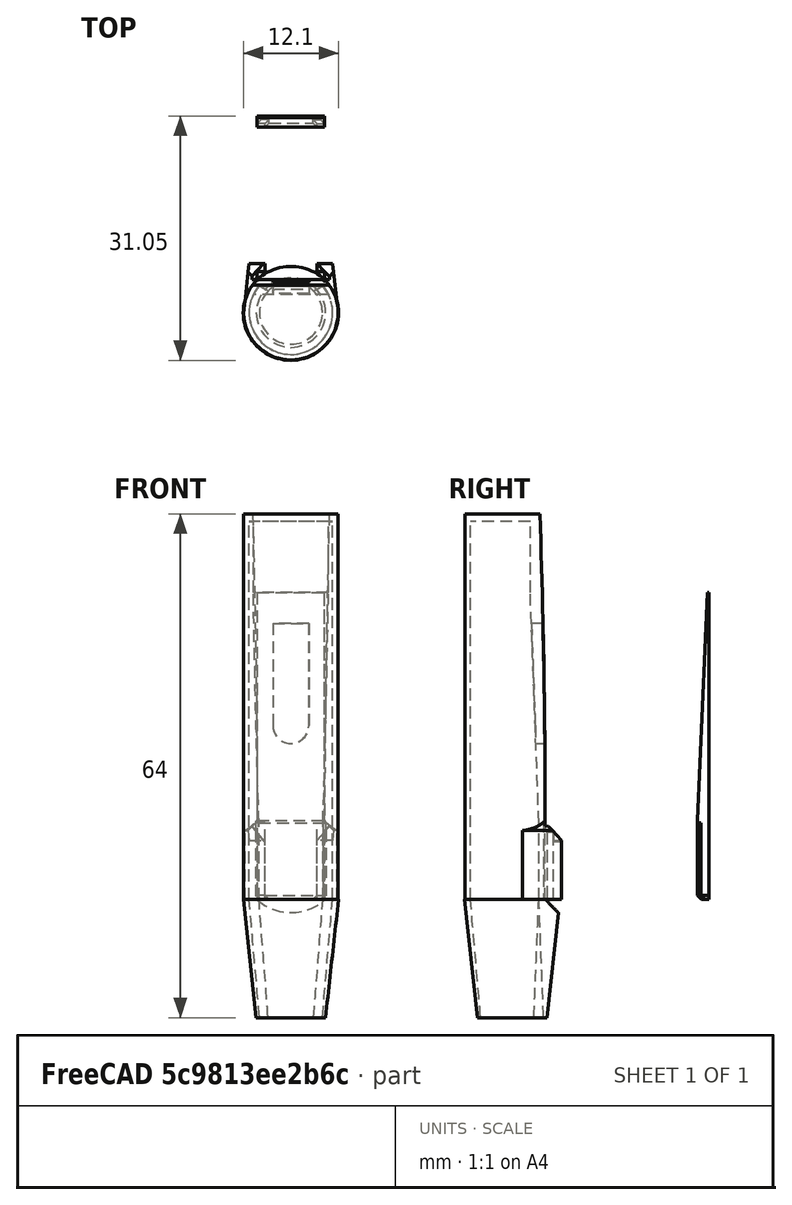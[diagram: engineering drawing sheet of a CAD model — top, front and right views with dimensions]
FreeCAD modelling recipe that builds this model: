
FCSTD DOCUMENT  (FreeCAD 1.0R39319 (Git))
Label: stroik
License: All rights reserved
LicenseURL: https://en.wikipedia.org/wiki/All_rights_reserved
objects: Sketcher::SketchObject×17, PartDesign::Pocket×10, PartDesign::Pad×4, PartDesign::Chamfer×3, App::VarSet×2, PartDesign::Body×2, Part::FeaturePython×1, PartDesign::FeatureBase×1, PartDesign::Mirrored×1, PartDesign::Plane×1, PartDesign::AdditiveLoft×1, PartDesign::ShapeBinder×1, Mesh::Feature×1
note: 97 computed .brp shape members not serialized (recipe doc carries the construction recipe); baked Part::Feature solids carry a one-line shape summary decoded from their .brp

FEATURE [Part::FeaturePython] Tube  # WARN: FeaturePython — macro-defined, semantics opaque (R4)
  AttacherType = Attacher::AttachEngine3D
  Height = 39
  InnerRadius = 5.3
  OuterRadius = 6
  Placement = pos=(0,0,0) rot=(0,1,0;1.5708rad)
  expr: Height = VarSet.leaf_len
  expr: InnerRadius = VarSet.d_inner
  expr: OuterRadius = VarSet.d_outer
FEATURE [PartDesign::FeatureBase] BaseFeature
  BaseFeature = -> Tube
  Suppressed = false
FEATURE [App::VarSet] VarSet
  d_inner = 5.3
  d_outer = 6
  d_outer_plug = 6.05
  leaf_end_thickness = 0.21
  leaf_gap = 1.5
  leaf_len = 39
  leaf_start_thickness = 1.44
  plug_inner_start = 4
  plug_len = 15
  plug_outer_start = 4.4
FEATURE [Sketcher::SketchObject] Sketch
  ArcFitTolerance = 1e-06
  AttachmentSupport = -> [YZ_Plane]
  ExternalGeometry = -> [BaseFeature]
  FullyConstrained = true
  MakeInternals = false
  MapMode = 5
  Placement = pos=(0,0,0) rot=(0.57735,0.57735,0.57735;2.0944rad)
  expr: Constraints[14] = VarSet.leaf_len / 4
  expr: Constraints[8] = VarSet.d_outer * 0.3
  sketch-geometry (6):
    g0: LineSegment StartX=6 StartY=39 StartZ=0 EndX=4.2 EndY=39 EndZ=0
    g1: LineSegment StartX=4.2 StartY=0 StartZ=0 EndX=6 EndY=0 EndZ=0
    g2: LineSegment StartX=6 StartY=0 StartZ=0 EndX=6 EndY=9.75 EndZ=0
    g3: LineSegment StartX=6 StartY=9.75 StartZ=0 EndX=6 EndY=39 EndZ=0
    g4: LineSegment StartX=4.2 StartY=39 StartZ=0 EndX=4.2 EndY=9.75 EndZ=0
    g5: LineSegment StartX=4.2 StartY=9.75 StartZ=0 EndX=4.2 EndY=0 EndZ=0
  constraints (17):
    c: Coincident(g0,g4)
    c: Coincident(g5,g1)
    c: Coincident(g1,g2)
    c: Coincident(g3,g0)
    c: Horizontal(g0)
    c: Horizontal(g1)
    c: Coincident(g0,g-3)
    c: PointOnObject(g5,g-4)
    c: DistanceX(g5,g1) = 1.8
    c: Coincident(g2,g3)
    c: Vertical(g2)
    c: Vertical(g3)
    c: Coincident(g4,g5)
    c: Vertical(g5)
    c: DistanceY(g2,g2) = 9.75
    c: Horizontal(g2,g4)
    c: Vertical(g4)
FEATURE [Sketcher::SketchObject] Sketch001
  ArcFitTolerance = 1e-06
  AttachmentSupport = -> [YZ_Plane]
  ExternalGeometry = -> [Sketch]
  FullyConstrained = true
  MakeInternals = false
  MapMode = 5
  Placement = pos=(0,0,0) rot=(0.57735,0.57735,0.57735;2.0944rad)
  expr: Constraints[12] = 0.8
  expr: Constraints[13] = VarSet.leaf_gap + 0.4 mm
  sketch-geometry (6):
    g0: LineSegment StartX=4.2 StartY=0 StartZ=0 EndX=3.4 EndY=0 EndZ=0
    g1: LineSegment StartX=3.4 StartY=0 StartZ=0 EndX=3.4 EndY=9.75 EndZ=0
    g2: LineSegment StartX=3.4 StartY=9.75 StartZ=0 EndX=2.3 EndY=39 EndZ=0
    g3: LineSegment StartX=2.3 StartY=39 StartZ=0 EndX=4.2 EndY=39 EndZ=0
    g4: LineSegment StartX=4.2 StartY=39 StartZ=0 EndX=4.2 EndY=9.75 EndZ=0
    g5: LineSegment StartX=4.2 StartY=9.75 StartZ=0 EndX=4.2 EndY=0 EndZ=0
  constraints (15):
    c: Coincident(g-4,g0)
    c: PointOnObject(g0,g-1)
    c: Coincident(g0,g1)
    c: Vertical(g1)
    c: Coincident(g1,g2)
    c: Coincident(g2,g3)
    c: Coincident(g3,g-3)
    c: Horizontal(g3)
    c: Coincident(g3,g4)
    c: Coincident(g4,g-4)
    c: Coincident(g4,g5)
    c: Coincident(g5,g0)
    c: DistanceX(g1,g4) = 0.8
    c: DistanceX(g2,g3) = 1.9
    c: Horizontal(g1,g4)
FEATURE [PartDesign::Pocket] Pocket  label="1 ścięcie"
  BaseFeature = -> BaseFeature
  Direction = (-1,0,0)
  Length = 5
  Length2 = 5
  Midplane = true
  Profile = -> Sketch
  ReferenceAxis = -> Sketch [N_Axis]
  Refine = true
  Suppressed = false
  Type = 1
FEATURE [PartDesign::Pad] Pad  label="uzupełnienie"
  AlongSketchNormal = false
  BaseFeature = -> Pocket
  Direction = (1,0,0)
  Length = 13
  Length2 = 10
  Midplane = true
  Profile = -> Sketch001
  ReferenceAxis = -> Sketch001 [N_Axis]
  Refine = true
  Suppressed = false
  Type = 1
  UpToShape = -> [Pocket]
FEATURE [PartDesign::Mirrored] Mirrored
  BaseFeature = -> Pad
  MirrorPlane = -> YZ_Plane
  Originals = -> [Pad]
  Refine = true
  Suppressed = false
  TransformMode = 0
FEATURE [Sketcher::SketchObject] Sketch002
  ArcFitTolerance = 1e-06
  AttachmentSupport = -> [Mirrored]
  ExternalGeometry = -> [Mirrored]
  FullyConstrained = true
  MakeInternals = false
  MapMode = 5
  Placement = pos=(0,4.2,0) rot=(0,0.707107,0.707107;3.14159rad)
  expr: Constraints[11] = VarSet.d_outer / 3
  expr: Constraints[8] = VarSet.leaf_len / 10
  expr: Constraints[9] = VarSet.leaf_len / 3
  sketch-geometry (4):
    g0: LineSegment StartX=2.28486 StartY=22.1 StartZ=0 EndX=2.28486 EndY=35.1 EndZ=0
    g1: LineSegment StartX=2.28486 StartY=35.1 StartZ=0 EndX=-2.28486 EndY=35.1 EndZ=0
    g2: LineSegment StartX=-2.28486 StartY=35.1 StartZ=0 EndX=-2.28486 EndY=22.1 EndZ=0
    g3: ArcOfCircle CenterX=0 CenterY=22.1 CenterZ=0 NormalX=0 NormalY=0 NormalZ=1 AngleXU=0 Radius=2.28486 StartAngle=3.14159 EndAngle=6.28319
  constraints (12):
    c: Coincident(g0,g1)
    c: Coincident(g1,g2)
    c: Coincident(g3,g2)
    c: Coincident(g3,g0)
    c: PointOnObject(g3,g-2)
    c: Horizontal(g0,g2)
    c: Horizontal(g2,g3)
    c: Symmetric(g0,g1,g-2)
    c: DistanceY(g1,g-7) = 3.9
    c: DistanceY(g3,g1) = 13
    c: Vertical(g1,g2)
    c: DistanceX(g0,g-6) = 2
FEATURE [PartDesign::Pocket] Pocket001  label="dziurka"
  BaseFeature = -> Mirrored
  Direction = (0,-1,2e-16)
  Length = 2.65
  Length2 = 5
  Profile = -> Sketch002
  ReferenceAxis = -> Sketch002 [N_Axis]
  Refine = true
  Suppressed = false
  Type = 0
  expr: Length = VarSet.d_inner / 2
FEATURE [Sketcher::SketchObject] Sketch003
  ArcFitTolerance = 1e-06
  AttachmentSupport = -> [Pocket001]
  ExternalGeometry = -> [Pocket001]
  FullyConstrained = true
  MakeInternals = false
  MapMode = 5
  Placement = pos=(0,0,39) rot=(0,0,1;0rad)
  sketch-geometry (2):
    g0: ArcOfCircle CenterX=0 CenterY=0 CenterZ=0 NormalX=0 NormalY=0 NormalZ=1 AngleXU=0 Radius=6 StartAngle=2.3662 EndAngle=7.05858
    g1: LineSegment StartX=-4.28486 StartY=4.2 StartZ=0 EndX=4.28486 EndY=4.2 EndZ=0
  constraints (5):
    c: Coincident(g0,g-1)
    c: Coincident(g0,g-4)
    c: Coincident(g1,g0)
    c: Coincident(g1,g0)
    c: Horizontal(g1)
FEATURE [PartDesign::Pad] Pad001  label="zaślepka"
  BaseFeature = -> Pocket001
  Direction = (0,0,1)
  Length = 10
  Length2 = 10
  Profile = -> Sketch003
  ReferenceAxis = -> Sketch003 [N_Axis]
  Refine = true
  Suppressed = false
  Type = 0
FEATURE [Sketcher::SketchObject] Sketch004
  ArcFitTolerance = 1e-06
  AttachmentSupport = -> [Pad001]
  ExternalGeometry = -> [Pad001]
  FullyConstrained = true
  MakeInternals = false
  MapMode = 5
  Placement = pos=(0,0,0) rot=(1,0,0;3.14159rad)
  expr: Constraints[4] = VarSet.d_outer_plug
  expr: Constraints[7] = VarSet.d_inner
  sketch-geometry (3):
    g0: ArcOfCircle CenterX=0 CenterY=0 CenterZ=0 NormalX=0 NormalY=0 NormalZ=1 AngleXU=0 Radius=5.3 StartAngle=5.58672 EndAngle=10.1212
    g1: LineSegment StartX=-4.06571 StartY=-3.4 StartZ=0 EndX=4.06571 EndY=-3.4 EndZ=0
    g2: Circle CenterX=0 CenterY=0 CenterZ=0 NormalX=0 NormalY=0 NormalZ=1 AngleXU=0 Radius=6.05
  constraints (8):
    c: Coincident(g1,g0)
    c: Horizontal(g1)
    c: Coincident(g2,g0)
    c: Coincident(g-1,g0)
    c: Radius(g2) = 6.05
    c: Horizontal(g0,g-6)
    c: Coincident(g1,g0)
    c: Radius(g0) = 5.3
FEATURE [PartDesign::Plane] DatumPlane
  AttachmentOffset = pos=(0,0,15) rot=(0,0,1;0rad)
  AttachmentSupport = -> [Pocket001]
  Length = 60
  MapMode = 5
  Placement = pos=(0,0,-15) rot=(1,0,0;3.14159rad)
  ResizeMode = 0
  Width = 60
  expr: .AttachmentOffset.Base.z = VarSet.plug_len
FEATURE [Sketcher::SketchObject] Sketch005
  ArcFitTolerance = 1e-06
  AttachmentSupport = -> [DatumPlane]
  ExternalGeometry = -> [Sketch004,Pad001]
  FullyConstrained = true
  MakeInternals = false
  MapMode = 5
  Placement = pos=(0,0,-15) rot=(1,0,0;3.14159rad)
  expr: Constraints[2] = VarSet.plug_inner_start
  expr: Constraints[3] = VarSet.plug_outer_start
  sketch-geometry (2):
    g0: Circle CenterX=0 CenterY=0 CenterZ=0 NormalX=0 NormalY=0 NormalZ=1 AngleXU=0 Radius=4
    g1: Circle CenterX=0 CenterY=0 CenterZ=0 NormalX=0 NormalY=0 NormalZ=1 AngleXU=0 Radius=4.4
  constraints (4):
    c: Coincident(g0,g-1)
    c: Coincident(g1,g0)
    c: Radius(g0) = 4
    c: Radius(g1) = 4.4
FEATURE [PartDesign::AdditiveLoft] AdditiveLoft  label="dziubek"
  BaseFeature = -> Pad001
  Closed = false
  Profile = -> Sketch005
  Refine = true
  Ruled = false
  Sections = -> [Sketch004]
  Suppressed = false
FEATURE [Sketcher::SketchObject] Sketch006
  ArcFitTolerance = 1e-06
  AttachmentSupport = -> [Pad001]
  ExternalGeometry = -> [Pad001]
  FullyConstrained = false
  MakeInternals = false
  MapMode = 5
  Placement = pos=(0,0,0) rot=(1,0,0;3.14159rad)
  expr: Constraints[24] = 1.05 mm
  sketch-geometry (16):
    g0: LineSegment StartX=4.28486 StartY=-4.2 StartZ=0 EndX=6 EndY=0 EndZ=0
    g1: LineSegment StartX=6 StartY=0 StartZ=0 EndX=5.28986 EndY=-6.25 EndZ=0
    g2: LineSegment StartX=5.28986 StartY=-6.25 StartZ=0 EndX=3.28986 EndY=-6.25 EndZ=0
    g3: LineSegment StartX=3.28986 StartY=-6.25 StartZ=0 EndX=3.28986 EndY=-5.25 EndZ=0
    g4: LineSegment StartX=3.28986 StartY=-5.25 StartZ=0 EndX=4.28986 EndY=-5.25 EndZ=0
    g5: LineSegment StartX=-5.28986 StartY=-6.25 StartZ=0 EndX=-3.28986 EndY=-6.25 EndZ=0
    g6: LineSegment StartX=-6 StartY=0 StartZ=0 EndX=-5.28986 EndY=-6.25 EndZ=0
    g7: LineSegment StartX=-4.28486 StartY=-4.2 StartZ=0 EndX=-6 EndY=0 EndZ=0
    g8: LineSegment StartX=-3.28986 StartY=-5.25 StartZ=0 EndX=-4.28986 EndY=-5.25 EndZ=0
    g9: LineSegment StartX=-3.28986 StartY=-6.25 StartZ=0 EndX=-3.28986 EndY=-5.25 EndZ=0
    g10: LineSegment StartX=4.28986 StartY=-5.25 StartZ=0 EndX=4.28986 EndY=-4.2 EndZ=0
    g11: LineSegment StartX=-4.28986 StartY=-5.25 StartZ=0 EndX=-4.28986 EndY=-4.2 EndZ=0
    g12: LineSegment StartX=4.28986 StartY=-4.2 StartZ=0 EndX=4.28717 EndY=-4.19654 EndZ=0
    g13: LineSegment StartX=4.28717 StartY=-4.19654 StartZ=0 EndX=4.28486 EndY=-4.2 EndZ=0
    g14: LineSegment StartX=-4.28986 StartY=-4.2 StartZ=0 EndX=-4.28627 EndY=-4.19642 EndZ=0
    g15: LineSegment StartX=-4.28627 StartY=-4.19642 StartZ=0 EndX=-4.28486 EndY=-4.2 EndZ=0
  constraints (36):
    c: Coincident(g-5,g0)
    c: Coincident(g0,g1)
    c: Coincident(g1,g2)
    c: Horizontal(g2)
    c: Coincident(g2,g3)
    c: Vertical(g3)
    c: Coincident(g3,g4)
    c: Horizontal(g4)
    c: Coincident(g4,g10)
    c: Coincident(g13,g0)
    c: Coincident(g7,g6)
    c: Coincident(g6,g5)
    c: Coincident(g5,g9)
    c: Vertical(g9)
    c: Coincident(g9,g8)
    c: Horizontal(g8)
    c: Coincident(g8,g11)
    c: Coincident(g15,g7)
    c: Symmetric(g2,g5,g-2)
    c: DistanceX(g4,g4) = 1
    c: Symmetric(g4,g11,g-2)
    c: Symmetric(g0,g6,g-2)
    c: DistanceY(g3,g3) = 1
    c: Symmetric(g7,g0,g-2)
    c: DistanceY(g10,g13) = 1.05
    c: DistanceX(g2,g2) = 2
    c: Coincident(g0,g-5)
    c: Symmetric(g5,g1,g-2)
    c: Coincident(g10,g12)
    c: Vertical(g10)
    c: Horizontal(g10,g0)
    c: DistanceX(g13,g12) = 0.005
    c: Coincident(g11,g14)
    c: Symmetric(g11,g10,g-2)
    c: Coincident(g12,g13)
    c: Coincident(g14,g15)
FEATURE [PartDesign::Pad] Pad002  label="uchwyt na listek"
  BaseFeature = -> AdditiveLoft
  Direction = (0,0,-1)
  Length = 9.75
  Length2 = 10
  Profile = -> Sketch006
  ReferenceAxis = -> Sketch006 [N_Axis]
  Refine = true
  Reversed = true
  Suppressed = false
  Type = 0
  expr: Length = VarSet.leaf_len / 4
FEATURE [Sketcher::SketchObject] Sketch009
  ArcFitTolerance = 1e-06
  AttachmentSupport = -> [YZ_Plane]
  ExternalGeometry = -> [Pad001]
  FullyConstrained = false
  MakeInternals = false
  MapMode = 5
  Placement = pos=(0,0,0) rot=(0.57735,0.57735,0.57735;2.0944rad)
  expr: .Constraints.gap = VarSet.leaf_gap
  expr: Constraints[19] = 3 / 4 * VarSet.leaf_len * 3 / 2
  expr: Constraints[1] = VarSet.leaf_len / 4
  expr: Constraints[20] = 3 / 4 * VarSet.leaf_len * 3
  sketch-geometry (13):
    g0: GeomPoint X=4.2 Y=9.75 Z=0
    g1: Circle [constr] CenterX=4.2 CenterY=9.75 CenterZ=0 NormalX=0 NormalY=0 NormalZ=1 AngleXU=0 Radius=1
    g2: Circle [constr] CenterX=4.2 CenterY=53.625 CenterZ=0 NormalX=0 NormalY=0 NormalZ=1 AngleXU=0 Radius=1
    g3: Circle [constr] CenterX=0.846497 CenterY=97.5 CenterZ=0 NormalX=0 NormalY=0 NormalZ=1 AngleXU=0 Radius=1
    g4: BSplineCurve PolesCount=3 KnotsCount=2 Degree=2 IsPeriodic=0
    g5: GeomPoint [constr] X=4.2 Y=9.75 Z=0
    g6: GeomPoint [constr] X=0.846497 Y=97.5 Z=0
    g7: LineSegment [constr] StartX=0.846497 StartY=97.5 StartZ=0 EndX=4.2 EndY=9.75 EndZ=0
    g8: LineSegment StartX=104.2 StartY=41.25 StartZ=0 EndX=104.2 EndY=9.75 EndZ=0
    g9: LineSegment StartX=104.2 StartY=9.75 StartZ=0 EndX=4.2 EndY=9.75 EndZ=0
    g10: LineSegment StartX=0.846497 StartY=97.5 StartZ=0 EndX=0.846497 EndY=90 EndZ=0
    g11: LineSegment StartX=0.846497 StartY=90 StartZ=0 EndX=104.2 EndY=41.25 EndZ=0
    g12: LineSegment [constr] StartX=4.2 StartY=49 StartZ=0 EndX=2.7 EndY=49 EndZ=0
  constraints (29):
    c: PointOnObject(g0,g-3)
    c: DistanceY(g-3,g0) = 9.75
    c: Weight(g1) = 1
    c: Equal(g1,g2)
    c: Equal(g1,g3)
    c: InternalAlignment(g1,g4)
    c: InternalAlignment(g2,g4)
    c: InternalAlignment(g3,g4)
    c: InternalAlignment(g5,g4)
    c: InternalAlignment(g6,g4)
    c: Coincident(g1,g0)
    c: Coincident(g7,g4)
    c: Coincident(g7,g4)
    c: Vertical(g8)
    c: Coincident(g8,g9)
    c: Coincident(g9,g0)
    c: Horizontal(g9)
    c: DistanceX(g9,g9) = 100
    c: Vertical(g-3,g2)
    c: DistanceY(g0,g2) = 43.875
    c: DistanceY(g0,g4) = 87.75
    c: Coincident(g10,g4)
    c: Vertical(g10)
    c: Coincident(g11,g10)
    c: Coincident(g11,g8)
    c: Coincident(g12,g-3)
    c: PointOnObject(g12,g7)
    c: Horizontal(g12)
    c: DistanceX(g12,g12) = 1.5  'gap'
FEATURE [PartDesign::Pocket] Pocket003  label="2 ścięcie"
  BaseFeature = -> Pad002
  Direction = (-1,0,0)
  Length = 100
  Length2 = 5
  Midplane = true
  Profile = -> Sketch009
  ReferenceAxis = -> Sketch009 [N_Axis]
  Refine = true
  Suppressed = false
  Type = 0
FEATURE [PartDesign::ShapeBinder] ShapeBinder
  Support = -> [Mirrored]
  TraceSupport = false
FEATURE [Sketcher::SketchObject] Sketch010  label="main shape"
  ArcFitTolerance = 1e-06
  AttachmentSupport = -> [XZ_Plane001]
  ExternalGeometry = -> [ShapeBinder]
  FullyConstrained = true
  MakeInternals = false
  MapMode = 5
  Placement = pos=(0,0,0) rot=(1,0,0;1.5708rad)
  expr: Constraints[6] = VarSet.leaf_len / 4
  expr: Constraints[9] = VarSet.leaf_len
  sketch-geometry (6):
    g0: LineSegment StartX=-4.28486 StartY=0 StartZ=0 EndX=4.28486 EndY=9e-16 EndZ=0
    g1: LineSegment StartX=4.28486 StartY=9e-16 StartZ=0 EndX=4.28486 EndY=9.75 EndZ=0
    g2: LineSegment StartX=-4.28486 StartY=9.75 StartZ=0 EndX=-4.28486 EndY=0 EndZ=0
    g3: LineSegment StartX=4.28486 StartY=9.75 StartZ=0 EndX=4.28486 EndY=39 EndZ=0
    g4: LineSegment StartX=-4.28486 StartY=9.75 StartZ=0 EndX=-4.28486 EndY=39 EndZ=0
    g5: LineSegment StartX=-4.28486 StartY=39 StartZ=0 EndX=4.28486 EndY=39 EndZ=0
  constraints (15):
    c: Coincident(g0,g1)
    c: Coincident(g2,g0)
    c: Vertical(g1)
    c: Vertical(g2)
    c: Coincident(g0,g-3)
    c: Coincident(g0,g-3)
    c: DistanceY(g1,g1) = 9.75
    c: Coincident(g3,g1)
    c: Symmetric(g3,g4,g-2)
    c: DistanceY(g0,g3) = 39
    c: Horizontal(g2,g1)
    c: Coincident(g4,g2)
    c: Coincident(g5,g4)
    c: Coincident(g5,g3)
    c: Vertical(g3)
FEATURE [PartDesign::Pad] Pad003
  Direction = (0,-1,2e-16)
  Length = 1.44
  Length2 = 10
  Placement = pos=(0,0,0) rot=(1,0,0;1.5708rad)
  Profile = -> Sketch010
  ReferenceAxis = -> Sketch010 [N_Axis]
  Refine = true
  Suppressed = false
  Type = 0
  expr: Length = VarSet.leaf_start_thickness
FEATURE [Sketcher::SketchObject] Sketch011
  ArcFitTolerance = 1e-06
  AttachmentSupport = -> [Pad003]
  ExternalGeometry = -> [Pad003]
  FullyConstrained = true
  MakeInternals = false
  MapMode = 5
  Placement = pos=(0,0,4e-16) rot=(1,0,0;3.14159rad)
  sketch-geometry (8):
    g0: LineSegment StartX=-3.28486 StartY=1.44 StartZ=0 EndX=-3.28486 EndY=1 EndZ=0
    g1: LineSegment StartX=-3.28486 StartY=1 StartZ=0 EndX=-8.28486 EndY=1 EndZ=0
    g2: LineSegment StartX=-8.28486 StartY=1 StartZ=0 EndX=-8.28486 EndY=4.94104 EndZ=0
    g3: LineSegment StartX=-8.28486 StartY=4.94104 StartZ=0 EndX=-3.28486 EndY=1.44 EndZ=0
    g4: LineSegment StartX=8.28486 StartY=4.94104 StartZ=0 EndX=3.28486 EndY=1.44 EndZ=0
    g5: LineSegment StartX=3.28486 StartY=1.44 StartZ=0 EndX=3.28486 EndY=1 EndZ=0
    g6: LineSegment StartX=3.28486 StartY=1 StartZ=0 EndX=8.28486 EndY=1 EndZ=0
    g7: LineSegment StartX=8.28486 StartY=1 StartZ=0 EndX=8.28486 EndY=4.94104 EndZ=0
  constraints (21):
    c: PointOnObject(g0,g-3)
    c: Vertical(g0)
    c: Coincident(g0,g1)
    c: Horizontal(g1)
    c: Coincident(g1,g2)
    c: Vertical(g2)
    c: Coincident(g2,g3)
    c: Coincident(g3,g0)
    c: DistanceX(g-4,g0) = 1
    c: Vertical(g5)
    c: Coincident(g5,g6)
    c: Coincident(g6,g7)
    c: Coincident(g7,g4)
    c: Coincident(g4,g5)
    c: Symmetric(g4,g0,g-2)
    c: Symmetric(g5,g0,g-2)
    c: Symmetric(g6,g1,g-2)
    c: Symmetric(g4,g2,g-2)
    c: DistanceY(g-5,g0) = 1
    c: Angle(g-3,g3) = 2.53073
    c: DistanceX(g1,g1) = 5
FEATURE [PartDesign::Pocket] Pocket004  label="uchwyt"
  BaseFeature = -> Pad003
  Direction = (0,0,1)
  Length = 9.75
  Length2 = 5
  Placement = pos=(0,0,0) rot=(1,0,0;1.5708rad)
  Profile = -> Sketch011
  ReferenceAxis = -> Sketch011 [N_Axis]
  Refine = true
  Suppressed = false
  Type = 0
  expr: Length = VarSet.leaf_len / 4
FEATURE [Sketcher::SketchObject] Sketch012
  ArcFitTolerance = 1e-06
  AttachmentSupport = -> [Pocket004]
  FullyConstrained = true
  MakeInternals = false
  MapMode = 5
  Placement = pos=(-4.28486,0,-2.78e-14) rot=(0.707107,0,-0.707107;3.14159rad)
  expr: Constraints[0] = VarSet.d_inner + 0.4 mm
  expr: Constraints[5] = VarSet.leaf_end_thickness
  sketch-geometry (3):
    g0: LineSegment StartX=-39.052 StartY=0.21 StartZ=0 EndX=-10.0388 EndY=1.44 EndZ=0
    g1: LineSegment StartX=-39.052 StartY=0.21 StartZ=0 EndX=-39.052 EndY=14.04 EndZ=0
    g2: LineSegment StartX=-39.052 StartY=14.04 StartZ=0 EndX=-10.0388 EndY=1.44 EndZ=0
  constraints (8):
    c: DistanceX(g0,g-3) = 5.7
    c: Coincident(g1,g0)
    c: Vertical(g1)
    c: Coincident(g2,g1)
    c: Coincident(g2,g0)
    c: DistanceY(g-4,g0) = 0.21
    c: Coincident(g0,g-3)
    c: DistanceY(g1,g1) = 13.83
FEATURE [PartDesign::Pocket] Pocket005  label="Pochylenie"
  BaseFeature = -> Pocket004
  Direction = (1,0,6.4e-15)
  Length = 5
  Length2 = 5
  Placement = pos=(0,0,0) rot=(1,0,0;1.5708rad)
  Profile = -> Sketch012
  ReferenceAxis = -> Sketch012 [N_Axis]
  Refine = true
  Suppressed = false
  Type = 1
FEATURE [PartDesign::Chamfer] Chamfer
  Angle = 45
  Base = -> Pocket003 [?Edge89,?Edge77]
  BaseFeature = -> Pocket003
  ChamferType = 0
  FlipDirection = false
  Refine = true
  Size = 2
  Size2 = 1
  SupportTransform = false
  Suppressed = true
  UseAllEdges = false
FEATURE [Sketcher::SketchObject] Sketch013
  ArcFitTolerance = 1e-06
  AttachmentSupport = -> [YZ_Plane]
  FullyConstrained = true
  MakeInternals = false
  MapMode = 5
  Placement = pos=(0,0,0) rot=(0.57735,0.57735,0.57735;2.0944rad)
  sketch-geometry (3):
    g0: LineSegment StartX=4.2 StartY=0 StartZ=0 EndX=18.3421 EndY=-14.1421 EndZ=0
    g1: LineSegment StartX=18.3421 StartY=-14.1421 StartZ=0 EndX=18.3421 EndY=1.8e-15 EndZ=0
    g2: LineSegment StartX=18.3421 StartY=1.8e-15 StartZ=0 EndX=4.2 EndY=0 EndZ=0
  constraints (8):
    c: Coincident(g-3,g0)
    c: Coincident(g0,g1)
    c: Vertical(g1)
    c: Coincident(g1,g2)
    c: Coincident(g2,g0)
    c: Angle(g-2,g0) = 0.785398
    c: Distance(g0,g0) = 20
    c: Angle(g0,g2) = 0.785398
FEATURE [PartDesign::Pocket] Pocket006
  BaseFeature = -> Chamfer
  Direction = (-1,0,0)
  Length = 5
  Length2 = 5
  Midplane = true
  Profile = -> Sketch013
  ReferenceAxis = -> Sketch013 [N_Axis]
  Refine = true
  Suppressed = false
  Type = 1
FEATURE [Sketcher::SketchObject] Sketch014
  ArcFitTolerance = 1e-06
  AttachmentSupport = -> [Pocket006]
  ExternalGeometry = -> [Mirrored]
  FullyConstrained = true
  MakeInternals = false
  MapMode = 5
  Placement = pos=(0,0,39) rot=(1,0,0;3.14159rad)
  sketch-geometry (2):
    g0: ArcOfCircle CenterX=0 CenterY=0 CenterZ=0 NormalX=0 NormalY=0 NormalZ=1 AngleXU=0 Radius=5.3 StartAngle=5.8343 EndAngle=9.87366
    g1: LineSegment StartX=4.77493 StartY=-2.3 StartZ=0 EndX=-4.77493 EndY=-2.3 EndZ=0
  constraints (5):
    c: Coincident(g0,g-1)
    c: Coincident(g0,g-4)
    c: Coincident(g1,g0)
    c: Coincident(g1,g0)
    c: Horizontal(g1)
FEATURE [PartDesign::Pocket] Pocket007
  BaseFeature = -> Pocket006
  Direction = (0,0,1)
  Length = 9
  Length2 = 5
  Profile = -> Sketch014
  ReferenceAxis = -> Sketch014 [N_Axis]
  Refine = true
  Suppressed = false
  Type = 0
FEATURE [App::VarSet] VarSet001  label="VarSet009"
  d_inner = 5.3
  d_outer = 6
  d_outer_plug = 6
  leaf_angle = 0
  leaf_angle2 = 1.6
  leaf_end_thickness = 0.2
  leaf_len = 39
  leaf_start_thickness = 1.45
  plug_inner_start = 4
  plug_len = 15
  plug_outer_start = 4.4
FEATURE [Sketcher::SketchObject] Sketch015
  ArcFitTolerance = 1e-06
  AttachmentSupport = -> [Pocket007]
  FullyConstrained = true
  MakeInternals = false
  MapMode = 5
  Placement = pos=(0,6.25,0) rot=(0,0.707107,0.707107;3.14159rad)
FEATURE [Sketcher::SketchObject] Sketch016
  ArcFitTolerance = 1e-06
  AttachmentSupport = -> [Pocket007]
  ExternalGeometry = -> [Pocket007]
  FullyConstrained = false
  MakeInternals = false
  MapMode = 5
  Placement = pos=(0,6.25,0) rot=(0,0.707107,0.707107;3.14159rad)
  sketch-geometry (6):
    g0: LineSegment StartX=-5.28986 StartY=9.75 StartZ=0 EndX=-2.018 EndY=6.06813 EndZ=0
    g1: LineSegment StartX=-2.018 StartY=6.06813 StartZ=0 EndX=-2.018 EndY=11.9722 EndZ=0
    g2: LineSegment StartX=-2.018 StartY=11.9722 StartZ=0 EndX=-5.28986 EndY=9.75 EndZ=0
    g3: LineSegment StartX=5.28986 StartY=9.75 StartZ=0 EndX=2.26844 EndY=6.06813 EndZ=0
    g4: LineSegment StartX=2.26844 StartY=6.06813 StartZ=0 EndX=2.26844 EndY=11.9722 EndZ=0
    g5: LineSegment StartX=2.26844 StartY=11.9722 StartZ=0 EndX=5.28986 EndY=9.75 EndZ=0
  constraints (12):
    c: Coincident(g-3,g0)
    c: Coincident(g0,g1)
    c: Vertical(g1)
    c: Coincident(g1,g2)
    c: Coincident(g2,g0)
    c: Coincident(g-4,g3)
    c: Coincident(g3,g4)
    c: Vertical(g4)
    c: Coincident(g4,g5)
    c: Coincident(g5,g3)
    c: Horizontal(g0,g3)
    c: Horizontal(g1,g4)
FEATURE [PartDesign::Pocket] Pocket008
  BaseFeature = -> Pocket007
  Direction = (0,-1,2e-16)
  Length = 5
  Length2 = 5
  Profile = -> Sketch016
  ReferenceAxis = -> Sketch016 [N_Axis]
  Refine = true
  Suppressed = false
  Type = 2
FEATURE [Sketcher::SketchObject] Sketch017
  ArcFitTolerance = 1e-06
  AttachmentSupport = -> [Pocket008]
  FullyConstrained = false
  MakeInternals = false
  MapMode = 5
  Placement = pos=(4.28986,0,0) rot=(0.57735,-0.57735,-0.57735;2.0944rad)
  sketch-geometry (3):
    g0: LineSegment StartX=-4.21102 StartY=9.75787 StartZ=0 EndX=-7.69576 EndY=5.94234 EndZ=0
    g1: LineSegment StartX=-7.69576 StartY=5.94234 StartZ=0 EndX=-7.9348 EndY=11.8707 EndZ=0
    g2: LineSegment StartX=-7.9348 StartY=11.8707 StartZ=0 EndX=-4.21102 EndY=9.75787 EndZ=0
  constraints (3):
    c: Coincident(g0,g1)
    c: Coincident(g1,g2)
    c: Coincident(g2,g0)
FEATURE [PartDesign::Pocket] Pocket009
  BaseFeature = -> Pocket008
  Direction = (1,0,0)
  Length = 5
  Length2 = 5
  Midplane = true
  Profile = -> Sketch017
  ReferenceAxis = -> Sketch017 [N_Axis]
  Refine = true
  Suppressed = false
  Type = 1
FEATURE [PartDesign::Chamfer] Chamfer001
  Angle = 45
  Base = -> Pocket009 [Edge62,Edge80]
  BaseFeature = -> Pocket009
  ChamferType = 0
  FlipDirection = false
  Refine = true
  Size = 1
  Size2 = 1
  SupportTransform = false
  Suppressed = false
  UseAllEdges = false
FEATURE [Sketcher::SketchObject] Sketch018
  ArcFitTolerance = 1e-06
  AttachmentSupport = -> [Chamfer001]
  ExternalGeometry = -> [Chamfer001]
  FullyConstrained = true
  MakeInternals = false
  MapMode = 5
  Placement = pos=(0,0,0) rot=(1,0,0;3.14159rad)
  sketch-geometry (2):
    g0: Circle CenterX=4.28986 CenterY=-4.2 CenterZ=0 NormalX=0 NormalY=0 NormalZ=1 AngleXU=0 Radius=0.2
    g1: Circle CenterX=-4.28986 CenterY=-4.2 CenterZ=0 NormalX=0 NormalY=0 NormalZ=1 AngleXU=0 Radius=0.2
  constraints (4):
    c: Coincident(g0,g-4)
    c: Diameter(g0) = 0.4
    c: Coincident(g1,g-3)
    c: Diameter(g1) = 0.4
FEATURE [PartDesign::Pocket] Pocket010
  BaseFeature = -> Chamfer001
  Direction = (0,0,1)
  Length = 10
  Length2 = 5
  Profile = -> Sketch018
  ReferenceAxis = -> Sketch018 [N_Axis]
  Refine = true
  Suppressed = false
  Type = 0
FEATURE [PartDesign::Body] Body  label="stroik"
  AllowCompound = false
  BaseFeature = -> Tube
  Group = -> [BaseFeature,Sketch,Pocket,Sketch001,Pad,Mirrored,Sketch002,Pocket001,Sketch003,Pad001,Sketch004,DatumPlane,Sketch005,AdditiveLoft,Sketch006,Pad002,Sketch009,Pocket003,Chamfer,Sketch013,Pocket006,Sketch014,Pocket007,Sketch015,Sketch016,Pocket008,Sketch017,Pocket009,Chamfer001,Sketch018,Pocket010]
  Origin = -> Origin
  Tip = -> Pocket010
FEATURE [PartDesign::Chamfer] Chamfer002
  Angle = 45
  Base = -> Pocket005 [Edge7,Edge6,Edge5,Edge4,Edge3,Edge8,Edge2]
  BaseFeature = -> Pocket005
  ChamferType = 0
  FlipDirection = false
  Placement = pos=(0,0,0) rot=(1,0,0;1.5708rad)
  Refine = true
  Size = 0.5
  Size2 = 1
  SupportTransform = false
  Suppressed = false
  UseAllEdges = false
FEATURE [PartDesign::Body] Body001  label="listek"
  AllowCompound = false
  Group = -> [ShapeBinder,Sketch010,Pad003,Sketch011,Pocket004,Sketch012,Pocket005,Chamfer002]
  Origin = -> Origin001
  Placement = pos=(0,25,0) rot=(0,0,1;0rad)
  Tip = -> Chamfer002
FEATURE [Mesh::Feature] Mesh  label="stroik (Meshed)"
